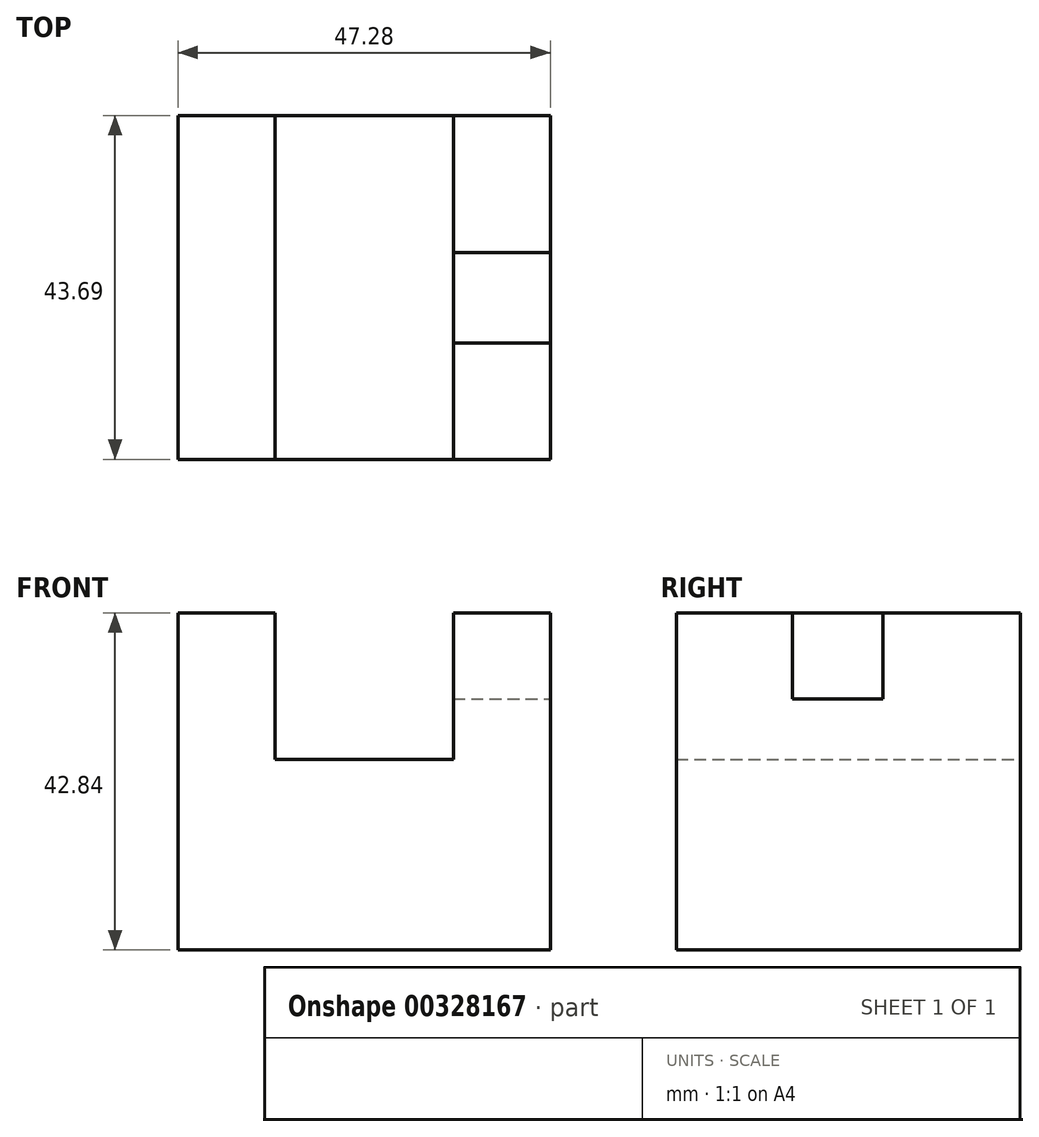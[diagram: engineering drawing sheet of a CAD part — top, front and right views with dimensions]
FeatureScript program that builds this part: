
annotation { "Feature Type Name" : "Feature", "Feature Type Description" : "" }
export const myFeature = defineFeature(function(context is Context, id is Id, definition is map)
    precondition{}
    {
        {
            var Q0;
            Q0=qCreatedBy(makeId("Front.planeOp"),FACE);
            var sketch = newSketch(context, id + "F0", { "sketchPlane" : qUnion([Q0])});
            skLineSegment(sketch, "E0.bottom", {"start": v(0, 0) * mm, "end": v(47.28, 0) * mm});
            skLineSegment(sketch, "E0.top", {"start": v(0, 42.84) * mm, "end": v(12.32, 42.84) * mm});
            skLineSegment(sketch, "E0.left", {"start": v(0, 0) * mm, "end": v(0, 42.84) * mm});
            skLineSegment(sketch, "E0.right", {"start": v(47.28, 0) * mm, "end": v(47.28, 42.84) * mm});
            skLineSegment(sketch, "E1.top", {"start": v(12.32, 24.21) * mm, "end": v(34.96, 24.21) * mm});
            skLineSegment(sketch, "E1.left", {"start": v(12.32, 42.84) * mm, "end": v(12.32, 24.21) * mm});
            skLineSegment(sketch, "E1.right", {"start": v(34.96, 42.84) * mm, "end": v(34.96, 24.21) * mm});
            skLineSegment(sketch, "E2.trimOffspring", {"start": v(34.96, 42.84) * mm, "end": v(47.28, 42.84) * mm});
            skSolve(sketch);
        }
        {
            var Q0;
            Q0 = qSketchRegion(id + "F0", true);
            extrude(context, id + "F1", {"entities" : qUnion([Q0]), "depth" : 43.69 * mm});
        }
        {
            var Q0;
            Q0=makeQuery(id+"F1.opExtrude","SWEPT_FACE",FACE,{"disambiguationData":[OSD([sQuery(id+"F0.wireOp",EDGE,"E2.trimOffspring")])]});
            var sketch = newSketch(context, id + "F2", { "sketchPlane" : qUnion([Q0])});
            skLineSegment(sketch, "E3.bottom", {"start": v(34.96, -28.94) * mm, "end": v(47.28, -28.94) * mm});
            skLineSegment(sketch, "E3.top", {"start": v(34.96, -17.45) * mm, "end": v(47.28, -17.45) * mm});
            skLineSegment(sketch, "E3.left", {"start": v(34.96, -28.94) * mm, "end": v(34.96, -17.45) * mm});
            skLineSegment(sketch, "E3.right", {"start": v(47.28, -28.94) * mm, "end": v(47.28, -17.45) * mm});
            skSolve(sketch);
        }
        {
            var Q0;
            Q0=makeQuery(id+"F2.imprint","IMPRINT",FACE,{"disambiguationData":[TD([[makeQuery(id+"F2.imprint","IMPRINT",EDGE,{"derivedFrom":sQuery(id+"F2.wireOp",EDGE,"E3.bottom")}),1.0]])]});
            extrude(context, id + "F3", {"entities" : qUnion([Q0]), "operationType" : NewBodyOperationType.REMOVE, "oppositeDirection" : true, "depth" : 10.92 * mm});
        }
    });
